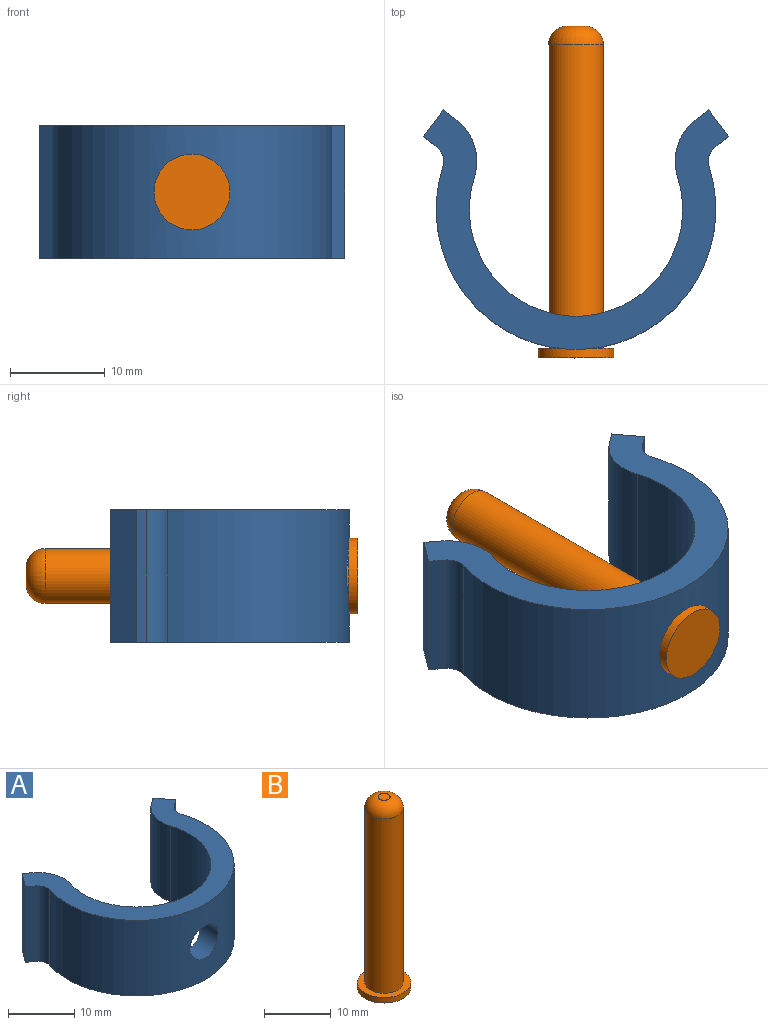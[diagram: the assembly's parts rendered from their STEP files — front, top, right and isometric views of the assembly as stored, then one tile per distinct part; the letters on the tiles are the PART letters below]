
ASSEMBLY  parts=2 mates=1
PART A: 15 faces, bbox 32.2x25.3x14 mm
  f0: cylinder r=2mm len=14mm, axis (0,0,-1), area 34.6mm2, adj f1,f11,f12,f13
  f1: cylinder r=14.75mm len=29.5mm, axis (0,0,-1), area 747.8mm2, adj f0,f2,f12,f13,f14
  f2: cylinder r=2mm len=14mm, axis (0,0,-1), area 34.6mm2, adj f1,f3,f12,f13
  f3: plane 14x1.34mm, normal (0.6,-0.8,0), area 23.5mm2, adj f2,f4,f12,f13
  f4: plane 14x2.8mm, normal (0.8,0.6,0), area 49mm2, adj f3,f5,f12,f13
  f5: plane 14x1.34mm, normal (-0.6,0.8,0), area 23.5mm2, adj f4,f6,f12,f13
  f6: cylinder r=5.5mm len=14mm, axis (0,0,-1), area 95.2mm2, adj f5,f7,f12,f13
  f7: cylinder r=11.25mm len=22.5mm, axis (0,0,-1), area 563.6mm2, adj f6,f8,f12,f13,f14
  f8: cylinder r=5.5mm len=14mm, axis (0,0,-1), area 95.2mm2, adj f7,f9,f12,f13
  f9: plane 14x1.34mm, normal (0.6,0.8,0), area 23.5mm2, adj f8,f10,f12,f13
  f10: plane 14x2.8mm, normal (-0.8,0.6,0), area 49mm2, adj f9,f11,f12,f13
  f11: plane 14x1.34mm, normal (-0.6,-0.8,0), area 23.5mm2, adj f0,f10,f12,f13
  f12: plane 32.2x25.25mm, normal (0,0,1), area 215.3mm2, adj f0,f1,f2,f3,f4,f5,f6,f7
  f13: plane 32.2x25.25mm, normal (0,0,-1), area 215.3mm2, adj f0,f1,f2,f3,f4,f5,f6,f7
  f14: cylinder r=3mm len=6mm, axis (0,-1,0), area 66.9mm2, adj f1,f7
PART B: 6 faces, bbox 8x8x35 mm
  f0: cylinder r=2.9mm len=32mm, axis (0,0,-1), area 583.1mm2, adj f2,f4
  f1: plane 1.8x1.8mm, normal (0,0,1), area 2.5mm2, adj f2
  f2: torus R=0.9mm, axis (0,0,1), area 42.9mm2, adj f0,f1
  f3: cylinder r=4mm len=8mm, axis (0,0,-1), area 25.1mm2, adj f4,f5
  f4: plane 8x8mm, normal (0,0,1), area 23.8mm2, adj f0,f3
  f5: plane 8x8mm, normal (0,0,-1), area 50.3mm2, adj f3
PLACE A t=(-2.51,0,-4.11)mm
PLACE B rot(axis=(-1,0,0),90deg) t=(-2.51,-15.64,-4.11)mm
MATE cylindrical B.f0 <-> A.f14  axis (0,-1,0) through (-2.51,-14.64,-4.11)mm
